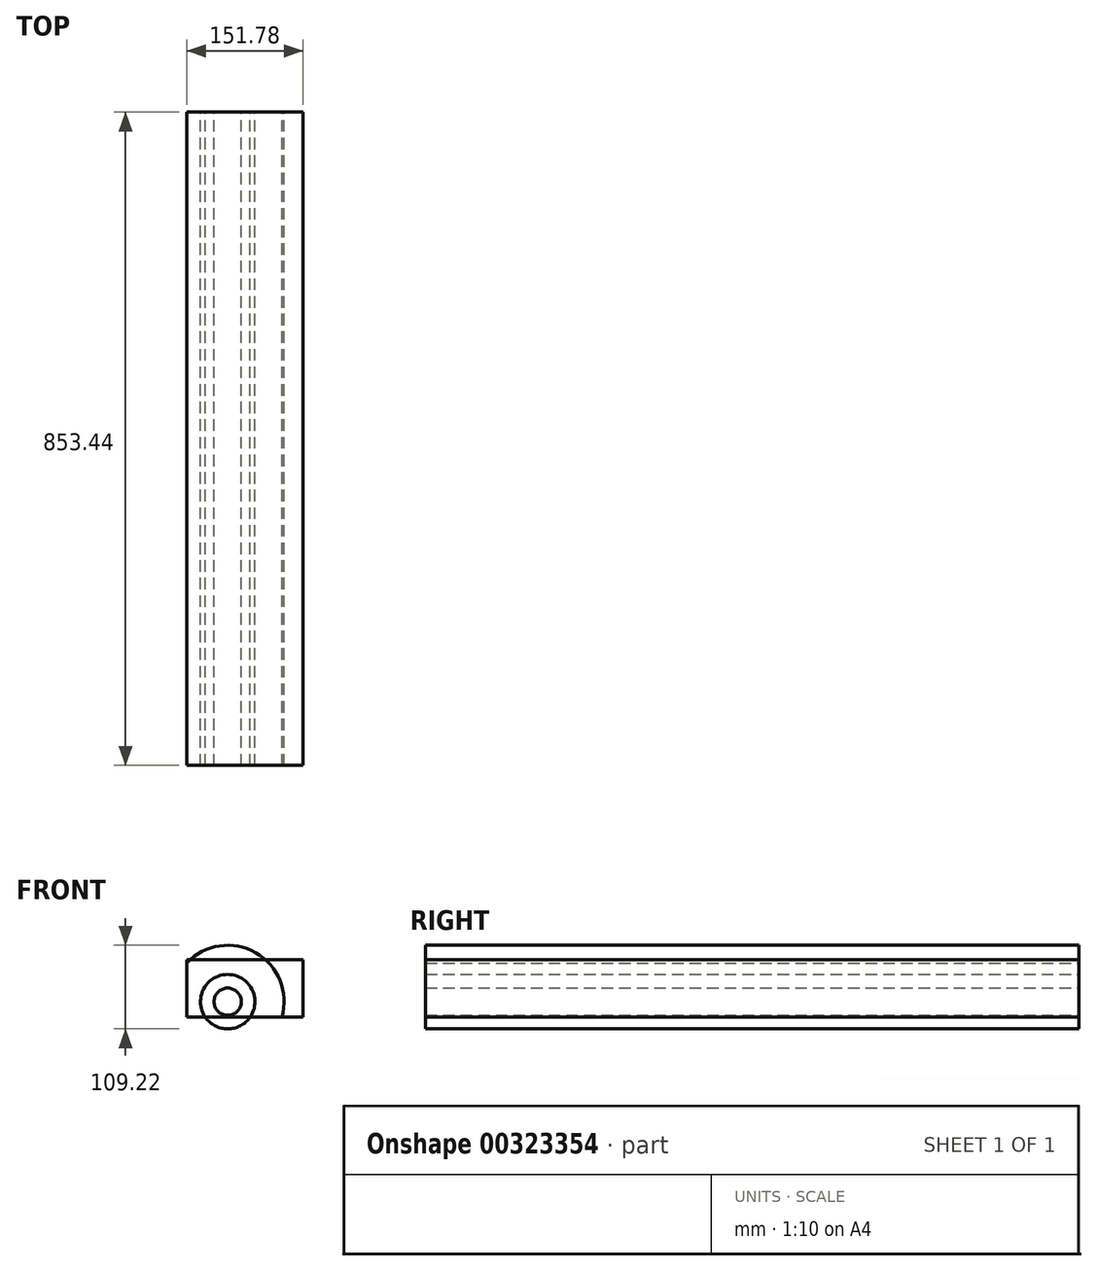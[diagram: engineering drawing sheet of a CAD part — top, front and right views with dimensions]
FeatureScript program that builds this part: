
annotation { "Feature Type Name" : "Feature", "Feature Type Description" : "" }
export const myFeature = defineFeature(function(context is Context, id is Id, definition is map)
    precondition{}
    {
        {
            var Q0;
            Q0=qCreatedBy(makeId("Front.planeOp"),FACE);
            var sketch = newSketch(context, id + "F0", { "sketchPlane" : qUnion([Q0])});
            skLineSegment(sketch, "E0", {"start": v(0, 0) * mm, "end": v(75.95, 0) * mm});
            skLineSegment(sketch, "E1", {"start": v(75.95, 0) * mm, "end": v(75.95, 75.36) * mm});
            skLineSegment(sketch, "E2", {"start": v(75.95, 75.36) * mm, "end": v(-75.83, 75.36) * mm});
            skLineSegment(sketch, "E3", {"start": v(-75.83, 75.36) * mm, "end": v(-75.83, -76.42) * mm});
            skLineSegment(sketch, "E4", {"start": v(-75.83, -76.42) * mm, "end": v(75.95, -76.42) * mm});
            skLineSegment(sketch, "E5", {"start": v(75.95, -76.42) * mm, "end": v(75.95, 0) * mm});
            skLineSegment(sketch, "E6", {"start": v(0, 0) * mm, "end": v(-75.83, 0) * mm});
            skSolve(sketch);
        }
        {
            var Q0;
            Q0=makeQuery(id+"F0.imprint","IMPRINT",FACE,{"disambiguationData":[TD([[makeQuery(id+"F0.imprint","IMPRINT",EDGE,{"derivedFrom":sQuery(id+"F0.wireOp",EDGE,"E0")}),1.0]])]});
            var sketch = newSketch(context, id + "F1", { "sketchPlane" : qUnion([Q0])});
            skCircle(sketch, "E7", {"center": v(-22.4, 20.23) * mm, "radius": 73.67 * mm});
            skCircle(sketch, "E8", {"center": v(-22.4, 20.23) * mm, "radius": 35.56 * mm});
            skCircle(sketch, "E9", {"center": v(-22.4, 20.23) * mm, "radius": 17.78 * mm});
            skCircle(sketch, "E10", {"center": v(-22.4, 20.23) * mm, "radius": 5.4 * mm});
            skSolve(sketch);
        }
        {
            var Q0;
            {var subQ0=sQuery(id+"F1.wireOp",EDGE,"E7");var subQ1=makeQuery(id+"F0.imprint","IMPRINT",EDGE,{"derivedFrom":sQuery(id+"F0.wireOp",EDGE,"E2")});var subQ2=makeQuery(id+"F1.imprint","INTERSECT",VERTEX,{"disambiguationData":[OD(0.0)],"derivedFrom":[subQ1,subQ0]});Q0=makeQuery(id+"F1.imprint","IMPRINT",FACE,{"disambiguationData":[TD([[makeQuery(id+"F1.imprint","IMPRINT",EDGE,{"disambiguationData":[TD([[subQ2,1.0]])],"derivedFrom":subQ0}),1.0]])]});}
            var Q1;
            {var subQ7=sQuery(id+"F0.wireOp",EDGE,"E2");var subQ10=sQuery(id+"F1.wireOp",EDGE,"E7");var subQ12=makeQuery(id+"F0.imprint","IMPRINT",EDGE,{"derivedFrom":subQ7});var subQ13=makeQuery(id+"F1.imprint","INTERSECT",VERTEX,{"disambiguationData":[OD(1.0)],"derivedFrom":[subQ12,subQ10]});Q1=makeQuery(id+"F1.imprint","IMPRINT",FACE,{"disambiguationData":[TD([[makeQuery(id+"F1.imprint","IMPRINT",EDGE,{"disambiguationData":[TD([[subQ13,1.0]])],"derivedFrom":subQ10}),1.0]])]});}
            var Q2;
            Q2=makeQuery(id+"F0.imprint","IMPRINT",FACE,{"disambiguationData":[TD([[makeQuery(id+"F0.imprint","IMPRINT",EDGE,{"derivedFrom":sQuery(id+"F0.wireOp",EDGE,"E0")}),1.0]])]});
            var Q3;
            Q3=makeQuery(id+"F1.imprint","IMPRINT",FACE,{"disambiguationData":[TD([[makeQuery(id+"F1.imprint","IMPRINT",EDGE,{"derivedFrom":sQuery(id+"F1.wireOp",EDGE,"E10")}),1.0]])]});
            var Q4;
            Q4=makeQuery(id+"F1.imprint","IMPRINT",FACE,{"disambiguationData":[TD([[makeQuery(id+"F1.imprint","IMPRINT",EDGE,{"derivedFrom":sQuery(id+"F1.wireOp",EDGE,"E9")}),1.0]])]});
            var Q5;
            {var subQ0=sQuery(id+"F1.wireOp",EDGE,"E8");var subQ1=makeQuery(id+"F0.imprint","IMPRINT",EDGE,{"derivedFrom":sQuery(id+"F0.wireOp",EDGE,"E0")});var subQ2=makeQuery(id+"F1.imprint","INTERSECT",VERTEX,{"derivedFrom":[subQ1,subQ0]});Q5=makeQuery(id+"F1.imprint","IMPRINT",FACE,{"disambiguationData":[TD([[makeQuery(id+"F1.imprint","IMPRINT",EDGE,{"disambiguationData":[TD([[subQ2,1.0]])],"derivedFrom":subQ0}),1.0]])]});}
            extrude(context, id + "F2", {"entities" : qUnion([Q0, Q1, Q2, Q3, Q4, Q5]), "depth" : 853.44 * mm});
        }
    });
